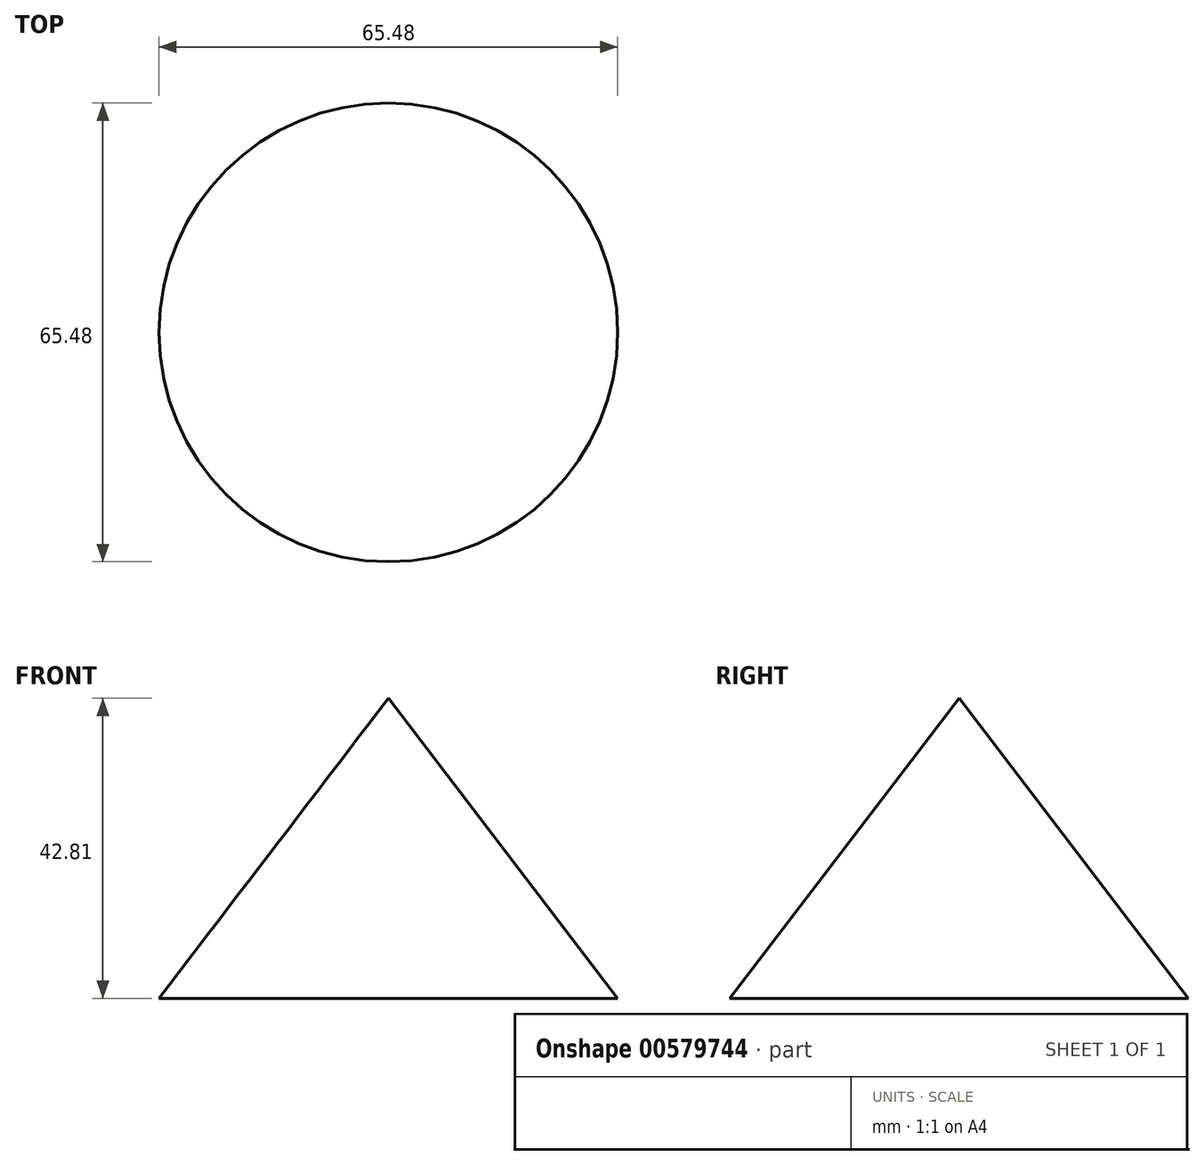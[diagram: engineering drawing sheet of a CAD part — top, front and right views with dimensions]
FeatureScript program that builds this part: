
annotation { "Feature Type Name" : "Feature", "Feature Type Description" : "" }
export const myFeature = defineFeature(function(context is Context, id is Id, definition is map)
    precondition{}
    {
        {
            var Q0;
            Q0=qCreatedBy(makeId("Front.planeOp"),FACE);
            var sketch = newSketch(context, id + "F0", { "sketchPlane" : qUnion([Q0])});
            skLineSegment(sketch, "E0", {"start": v(0, 0) * mm, "end": v(32.74, 0) * mm});
            skLineSegment(sketch, "E1", {"start": v(32.74, 0) * mm, "end": v(0, 42.8) * mm});
            skLineSegment(sketch, "E2", {"start": v(0, 42.8) * mm, "end": v(0, 0) * mm});
            skSolve(sketch);
        }
        {
            var Q0;
            Q0=makeQuery(id+"F0.imprint","IMPRINT",FACE,{"disambiguationData":[TD([[makeQuery(id+"F0.imprint","IMPRINT",EDGE,{"derivedFrom":sQuery(id+"F0.wireOp",EDGE,"E0")}),1.0]])]});
            var Q1;
            Q1=sQuery(id+"F0.wireOp",EDGE,"E2");
            revolve(context, id + "F1", {"entities" : qUnion([Q0]), "axis" : qUnion([Q1]), "revolveType" : RevolveType.FULL});
        }
    });
